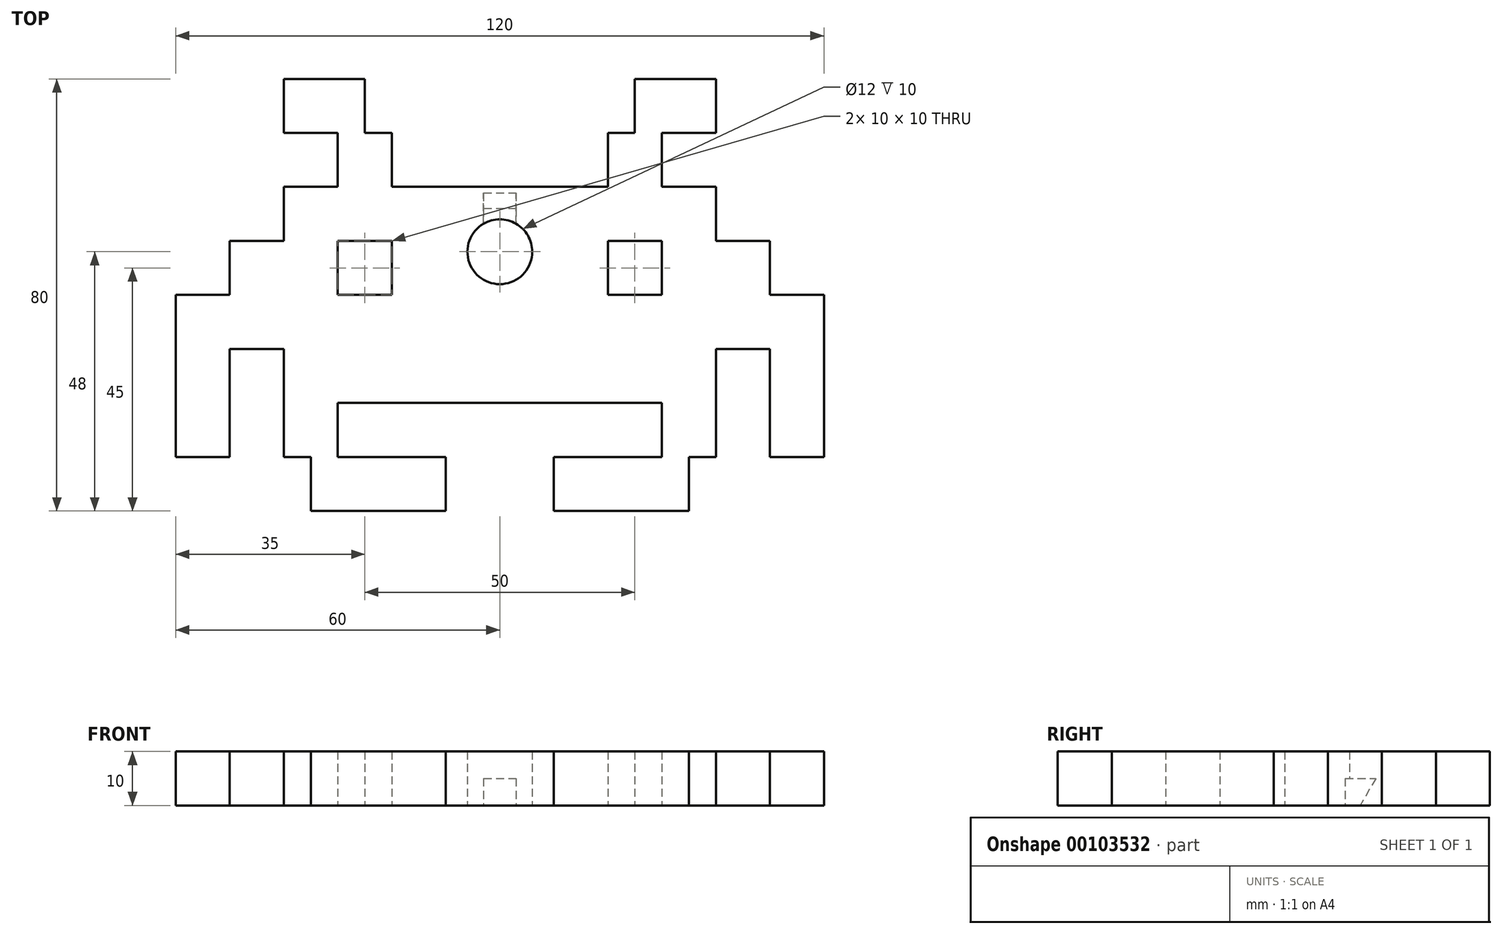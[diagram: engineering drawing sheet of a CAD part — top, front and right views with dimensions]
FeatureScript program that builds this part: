
annotation { "Feature Type Name" : "Feature", "Feature Type Description" : "" }
export const myFeature = defineFeature(function(context is Context, id is Id, definition is map)
    precondition{}
    {
        {
            var Q0;
            Q0=qCreatedBy(makeId("Top.planeOp"),FACE);
            var sketch = newSketch(context, id + "F0", { "sketchPlane" : qUnion([Q0]), "disableImprinting" : false});
            skLineSegment(sketch, "E0", {"start": v(0, 0) * mm, "end": v(-10, 0) * mm});
            skLineSegment(sketch, "E1", {"start": v(-20, 0) * mm, "end": v(-20, 10) * mm});
            skLineSegment(sketch, "E2", {"start": v(-20, 10) * mm, "end": v(-30, 10) * mm});
            skLineSegment(sketch, "E3", {"start": v(-30, 10) * mm, "end": v(-30, 20) * mm, "construction": true});
            skLineSegment(sketch, "E4", {"start": v(-30, 20) * mm, "end": v(-40, 20) * mm});
            skLineSegment(sketch, "E5", {"start": v(-40, 20) * mm, "end": v(-40, 10) * mm});
            skLineSegment(sketch, "E6", {"start": v(-40, 10) * mm, "end": v(-30, 10) * mm});
            skLineSegment(sketch, "E7", {"start": v(-30, 10) * mm, "end": v(-30, 0) * mm});
            skLineSegment(sketch, "E8", {"start": v(-30, 0) * mm, "end": v(-40, 0) * mm});
            skLineSegment(sketch, "E9", {"start": v(-40, 0) * mm, "end": v(-40, -10) * mm});
            skLineSegment(sketch, "E10", {"start": v(-40, -10) * mm, "end": v(-50, -10) * mm});
            skLineSegment(sketch, "E11", {"start": v(-40, -40) * mm, "end": v(-40, -50) * mm});
            skLineSegment(sketch, "E12", {"start": v(-40, -50) * mm, "end": v(-35, -50) * mm});
            skLineSegment(sketch, "E13", {"start": v(-30, -50) * mm, "end": v(-30, -40) * mm});
            skLineSegment(sketch, "E14", {"start": v(-30, -40) * mm, "end": v(-20, -40) * mm});
            skLineSegment(sketch, "E15", {"start": v(-10, 0) * mm, "end": v(-20, 0) * mm});
            skLineSegment(sketch, "E16", {"start": v(-10, -40) * mm, "end": v(0, -40) * mm});
            skLineSegment(sketch, "E17", {"start": v(-20, -40) * mm, "end": v(-10, -40) * mm});
            skLineSegment(sketch, "E18", {"start": v(-60, -20) * mm, "end": v(-60, -30) * mm});
            skLineSegment(sketch, "E19.bottom", {"start": v(-30, -10) * mm, "end": v(-20, -10) * mm});
            skLineSegment(sketch, "E19.top", {"start": v(-30, -20) * mm, "end": v(-20, -20) * mm});
            skLineSegment(sketch, "E19.left", {"start": v(-30, -10) * mm, "end": v(-30, -20) * mm});
            skLineSegment(sketch, "E19.right", {"start": v(-20, -10) * mm, "end": v(-20, -20) * mm});
            skLineSegment(sketch, "E20", {"start": v(-30, 20) * mm, "end": v(-25, 20) * mm});
            skLineSegment(sketch, "E21", {"start": v(-25, 20) * mm, "end": v(-25, 10) * mm});
            skLineSegment(sketch, "E22", {"start": v(-40, -40) * mm, "end": v(-40, -30) * mm});
            skLineSegment(sketch, "E23", {"start": v(-50, -10) * mm, "end": v(-50, -20) * mm});
            skLineSegment(sketch, "E24", {"start": v(-50, -20) * mm, "end": v(-60, -20) * mm});
            skLineSegment(sketch, "E25", {"start": v(-40, -30) * mm, "end": v(-50, -30) * mm});
            skLineSegment(sketch, "E26", {"start": v(-50, -30) * mm, "end": v(-50, -50) * mm});
            skLineSegment(sketch, "E27", {"start": v(-50, -50) * mm, "end": v(-60, -50) * mm});
            skLineSegment(sketch, "E28", {"start": v(-60, -50) * mm, "end": v(-60, -30) * mm});
            skLineSegment(sketch, "E29.bottom", {"start": v(-10, -50) * mm, "end": v(-35, -50) * mm});
            skLineSegment(sketch, "E29.top", {"start": v(-10, -60) * mm, "end": v(-35, -60) * mm});
            skLineSegment(sketch, "E29.left", {"start": v(-10, -50) * mm, "end": v(-10, -60) * mm});
            skLineSegment(sketch, "E29.right", {"start": v(-35, -50) * mm, "end": v(-35, -60) * mm});
            skLineSegment(sketch, "E30", {"start": v(-35, -50) * mm, "end": v(-30, -50) * mm, "construction": true});
            skLineSegment(sketch, "E31.MirrorCS", {"start": v(40, -50) * mm, "end": v(35, -50) * mm});
            skLineSegment(sketch, "E32.MirrorCS", {"start": v(30, 10) * mm, "end": v(30, 20) * mm, "construction": true});
            skLineSegment(sketch, "E33.MirrorCS", {"start": v(35, -50) * mm, "end": v(30, -50) * mm, "construction": true});
            skLineSegment(sketch, "E34.MirrorCS", {"start": v(30, 20) * mm, "end": v(25, 20) * mm});
            skLineSegment(sketch, "E35.MirrorCS", {"start": v(20, 10) * mm, "end": v(30, 10) * mm});
            skLineSegment(sketch, "E36.MirrorCS", {"start": v(10, -50) * mm, "end": v(35, -50) * mm});
            skLineSegment(sketch, "E37.MirrorCS", {"start": v(0, 0) * mm, "end": v(10, 0) * mm});
            skLineSegment(sketch, "E38.MirrorCS", {"start": v(20, 0) * mm, "end": v(20, 10) * mm});
            skLineSegment(sketch, "E39.MirrorCS", {"start": v(40, 10) * mm, "end": v(30, 10) * mm});
            skLineSegment(sketch, "E40.MirrorCS", {"start": v(40, -10) * mm, "end": v(50, -10) * mm});
            skLineSegment(sketch, "E41.MirrorCS", {"start": v(10, -60) * mm, "end": v(35, -60) * mm});
            skLineSegment(sketch, "E42.MirrorCS", {"start": v(30, -40) * mm, "end": v(20, -40) * mm});
            skLineSegment(sketch, "E43.MirrorCS", {"start": v(40, 20) * mm, "end": v(40, 10) * mm});
            skLineSegment(sketch, "E44.MirrorCS", {"start": v(20, -40) * mm, "end": v(10, -40) * mm});
            skLineSegment(sketch, "E45.MirrorCS", {"start": v(50, -10) * mm, "end": v(50, -20) * mm});
            skLineSegment(sketch, "E46.MirrorCS", {"start": v(30, -50) * mm, "end": v(30, -40) * mm});
            skLineSegment(sketch, "E47.MirrorCS", {"start": v(30, 10) * mm, "end": v(30, 0) * mm});
            skLineSegment(sketch, "E48.MirrorCS", {"start": v(10, -50) * mm, "end": v(10, -60) * mm});
            skLineSegment(sketch, "E49.MirrorCS", {"start": v(30, -10) * mm, "end": v(20, -10) * mm});
            skLineSegment(sketch, "E50.MirrorCS", {"start": v(10, -40) * mm, "end": v(0, -40) * mm});
            skLineSegment(sketch, "E51.MirrorCS", {"start": v(35, -50) * mm, "end": v(35, -60) * mm});
            skLineSegment(sketch, "E52.MirrorCS", {"start": v(30, 20) * mm, "end": v(40, 20) * mm});
            skLineSegment(sketch, "E53.MirrorCS", {"start": v(50, -20) * mm, "end": v(60, -20) * mm});
            skLineSegment(sketch, "E54.MirrorCS", {"start": v(30, -20) * mm, "end": v(20, -20) * mm});
            skLineSegment(sketch, "E55.MirrorCS", {"start": v(50, -30) * mm, "end": v(50, -50) * mm});
            skLineSegment(sketch, "E56.MirrorCS", {"start": v(40, -40) * mm, "end": v(40, -30) * mm});
            skLineSegment(sketch, "E57.MirrorCS", {"start": v(40, -30) * mm, "end": v(50, -30) * mm});
            skLineSegment(sketch, "E58.MirrorCS", {"start": v(30, -10) * mm, "end": v(30, -20) * mm});
            skLineSegment(sketch, "E59.MirrorCS", {"start": v(50, -50) * mm, "end": v(60, -50) * mm});
            skLineSegment(sketch, "E60.MirrorCS", {"start": v(20, -10) * mm, "end": v(20, -20) * mm});
            skLineSegment(sketch, "E61.MirrorCS", {"start": v(30, 0) * mm, "end": v(40, 0) * mm});
            skLineSegment(sketch, "E62.MirrorCS", {"start": v(40, 0) * mm, "end": v(40, -10) * mm});
            skLineSegment(sketch, "E63.MirrorCS", {"start": v(40, -40) * mm, "end": v(40, -50) * mm});
            skLineSegment(sketch, "E64.MirrorCS", {"start": v(60, -20) * mm, "end": v(60, -30) * mm});
            skLineSegment(sketch, "E65.MirrorCS", {"start": v(10, 0) * mm, "end": v(20, 0) * mm});
            skLineSegment(sketch, "E66.MirrorCS", {"start": v(25, 20) * mm, "end": v(25, 10) * mm});
            skLineSegment(sketch, "E67.MirrorCS", {"start": v(60, -50) * mm, "end": v(60, -30) * mm});
            skPoint(sketch, "E68", {"position": v(0, -12) * mm});
            skCircle(sketch, "E69", {"center": v(0, -12) * mm, "radius": 6 * mm});
            skSolve(sketch);
        }
        {
            var Q0;
            Q0 = qSketchRegion(id + "F0", true);
            extrude(context, id + "F1", {"entities" : qUnion([Q0]), "depth" : 10 * mm});
        }
        {
            var Q0;
            Q0=qCreatedBy(makeId("Right.planeOp"),FACE);
            var sketch = newSketch(context, id + "F2", { "sketchPlane" : qUnion([Q0])});
            skLineSegment(sketch, "E70", {"start": v(-10, 0) * mm, "end": v(-10, 5) * mm});
            skLineSegment(sketch, "E71", {"start": v(-10, 5) * mm, "end": v(-1.11, 5) * mm});
            skLineSegment(sketch, "E72", {"start": v(-1.11, 5) * mm, "end": v(-4, 0) * mm});
            skLineSegment(sketch, "E73", {"start": v(-4, 0) * mm, "end": v(-10, 0) * mm});
            skSolve(sketch);
        }
        {
            var Q0;
            Q0 = qSketchRegion(id + "F2", true);
            extrude(context, id + "F3", {"entities" : qUnion([Q0]), "operationType" : NewBodyOperationType.REMOVE, "oppositeDirection" : true, "depth" : 6 * mm, "symmetric" : true});
        }
    });
